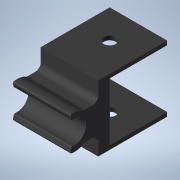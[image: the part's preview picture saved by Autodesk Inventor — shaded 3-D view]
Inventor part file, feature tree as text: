
AUTODESK INVENTOR PART (.ipt)
format: ipt  version: 2021 (Build 250183000, 183)  size: 162,304 bytes
history: native  units: mm
features: extrude x4, sketch x4, fillet x2, projected_geometry x2
ambient origin geometry x8: Origin, YZ Plane, XZ Plane, XY Plane, X Axis, Y Axis, Z Axis, Center Point
bodies: Solid1 (feature_tree)
feature tree (12):
  extrude  "Extrusion1"  Depth=4.0mm TaperAngle=0.0deg
  extrude  "Extrusion2"  Depth=10.0mm
  fillet  "Fillet1"  Radius=4.0mm
  fillet  "Fillet2"  Radius=10.0mm
  extrude  "Extrusion3"  Depth=20.0mm TaperAngle=0.0deg
  extrude  "Extrusion4"  Depth=0.5mm
  sketch  "Sketch1"  dims[d0=20.0mm d1=4.0mm d2=0.0mm]
  sketch  "Sketch2"  dims[d3=6.0mm d4=5.0mm d5=4.0mm d6=10.0mm]
  projected_geometry  "Projected Loop1"
  sketch  "Sketch4"  dims[d8=150.0deg d9=20.0mm d10=0.0mm]
  sketch  "Sketch5"  dims[d11=2.0mm d12=0.5mm d16=23.0mm d17=1.4mm d18=20.0mm d19=0.0mm d20=4.3mm d21=0.0mm d22=0.0mm]
  projected_geometry  "Projected Loop2"
